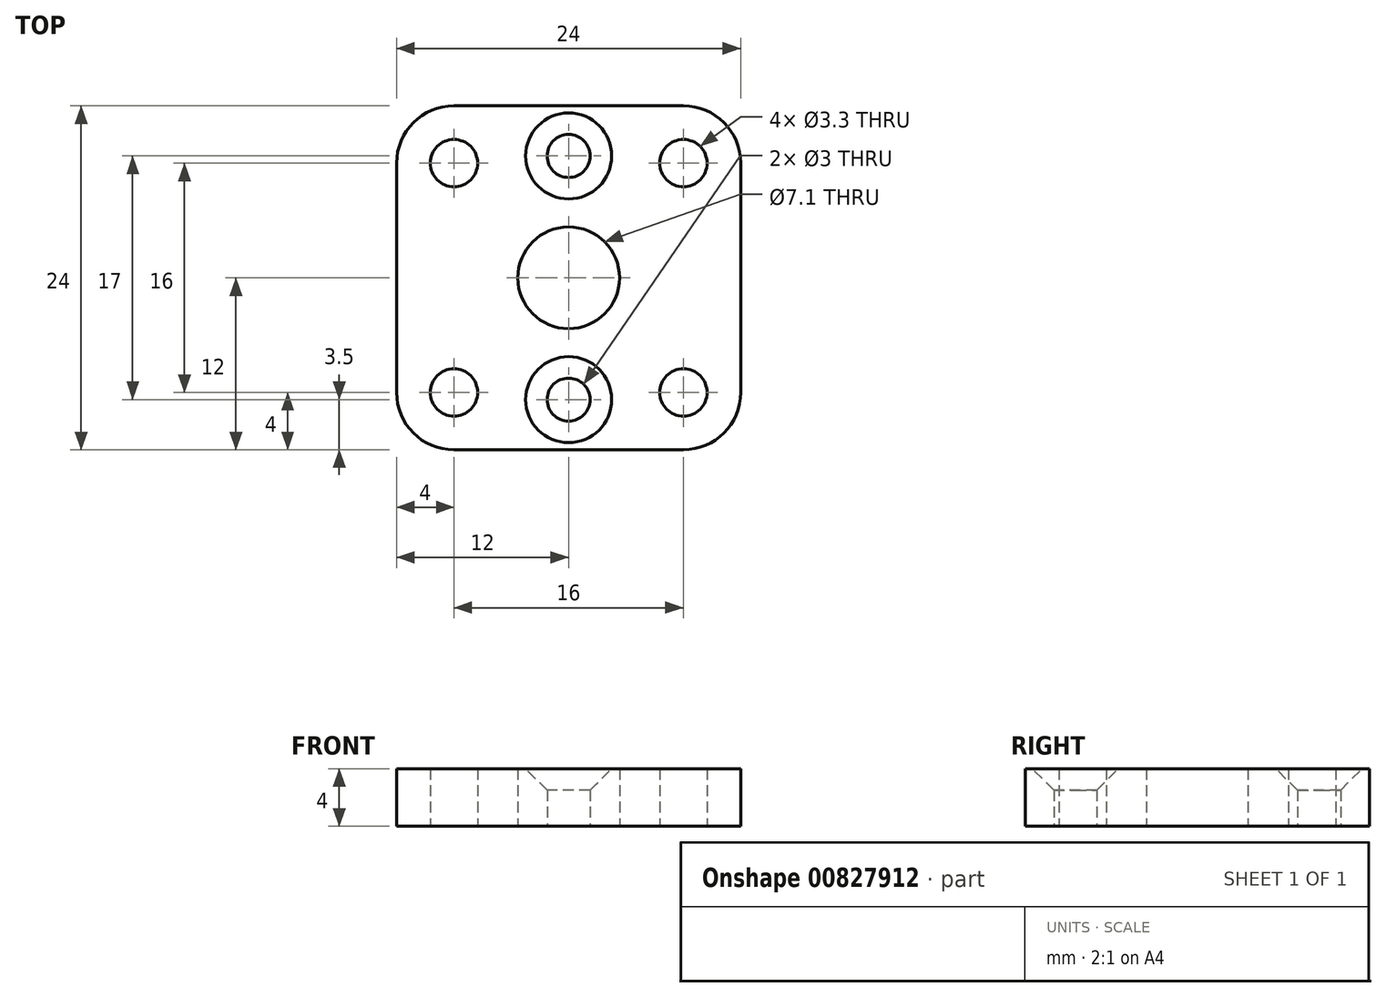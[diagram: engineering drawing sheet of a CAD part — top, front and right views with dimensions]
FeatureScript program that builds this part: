
annotation { "Feature Type Name" : "Feature", "Feature Type Description" : "" }
export const myFeature = defineFeature(function(context is Context, id is Id, definition is map)
    precondition{}
    {
        {
            var Q0;
            Q0=qCreatedBy(makeId("Top.planeOp"),FACE);
            var sketch = newSketch(context, id + "F0", { "sketchPlane" : qUnion([Q0])});
            skCircle(sketch, "E0", {"center": v(0, 0) * mm, "radius": 3.55 * mm});
            skCircle(sketch, "E1", {"center": v(0, 8.5) * mm, "radius": 1.5 * mm});
            skCircle(sketch, "E2", {"center": v(0, -8.5) * mm, "radius": 1.5 * mm});
            skLineSegment(sketch, "E3", {"start": v(0, 8.5) * mm, "end": v(0, 0) * mm, "construction": true});
            skLineSegment(sketch, "E4", {"start": v(0, 0) * mm, "end": v(0, -8.5) * mm, "construction": true});
            skLineSegment(sketch, "E5.bottom", {"start": v(-8, 8) * mm, "end": v(8, 8) * mm, "construction": true});
            skLineSegment(sketch, "E5.top", {"start": v(-8, -8) * mm, "end": v(8, -8) * mm, "construction": true});
            skLineSegment(sketch, "E5.left", {"start": v(-8, 8) * mm, "end": v(-8, -8) * mm, "construction": true});
            skLineSegment(sketch, "E5.right", {"start": v(8, 8) * mm, "end": v(8, -8) * mm, "construction": true});
            skCircle(sketch, "E6", {"center": v(8, 8) * mm, "radius": 1.65 * mm});
            skCircle(sketch, "E7", {"center": v(8, -8) * mm, "radius": 1.65 * mm});
            skCircle(sketch, "E8", {"center": v(-8, 8) * mm, "radius": 1.65 * mm});
            skCircle(sketch, "E9", {"center": v(-8, -8) * mm, "radius": 1.65 * mm});
            skLineSegment(sketch, "E10.bottom", {"start": v(8, 12) * mm, "end": v(-8, 12) * mm});
            skLineSegment(sketch, "E10.top", {"start": v(8, -12) * mm, "end": v(-8, -12) * mm});
            skLineSegment(sketch, "E10.left", {"start": v(12, 8) * mm, "end": v(12, -8) * mm});
            skLineSegment(sketch, "E10.right", {"start": v(-12, 8) * mm, "end": v(-12, -8) * mm});
            skPoint(sketch, "E11.visualSharp", {"position": v(-12, 12) * mm});
            skArc(sketch, "E11.filletArc", {"start": v(-8, 12) * mm, "mid": v(-10.83, 10.83) * mm, "end": v(-12, 8) * mm});
            skPoint(sketch, "E12.visualSharp", {"position": v(-12, -12) * mm});
            skArc(sketch, "E12.filletArc", {"start": v(-12, -8) * mm, "mid": v(-10.83, -10.83) * mm, "end": v(-8, -12) * mm});
            skPoint(sketch, "E13.visualSharp", {"position": v(12, -12) * mm});
            skArc(sketch, "E13.filletArc", {"start": v(8, -12) * mm, "mid": v(10.83, -10.83) * mm, "end": v(12, -8) * mm});
            skPoint(sketch, "E14.visualSharp", {"position": v(12, 12) * mm});
            skArc(sketch, "E14.filletArc", {"start": v(12, 8) * mm, "mid": v(10.83, 10.83) * mm, "end": v(8, 12) * mm});
            skSolve(sketch);
        }
        {
            var Q0;
            Q0 = qSketchRegion(id + "F0", true);
            extrude(context, id + "F1", {"entities" : qUnion([Q0]), "depth" : 4 * mm, "offsetDistance" : 25 * mm});
        }
        {
            var Q0;
            Q0=makeQuery(id+"F1.opExtrude","CAP_EDGE",EDGE,{"disambiguationData":[OSD([sQuery(id+"F0.wireOp",EDGE,"E1")])],"isStart":false});
            var Q1;
            Q1=makeQuery(id+"F1.opExtrude","CAP_EDGE",EDGE,{"disambiguationData":[OSD([sQuery(id+"F0.wireOp",EDGE,"E2")])],"isStart":false});
            chamfer(context, id + "F2", {"entities" : qUnion([Q0, Q1]), "chamferType" : ChamferType.OFFSET_ANGLE, "width" : 1.5 * mm, "oppositeDirection" : false, "angle" : 45 * degree, "tangentPropagation" : true});
        }
    });
